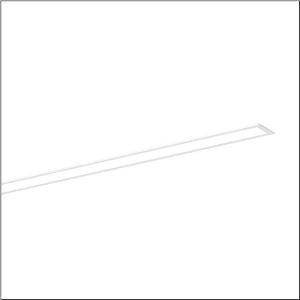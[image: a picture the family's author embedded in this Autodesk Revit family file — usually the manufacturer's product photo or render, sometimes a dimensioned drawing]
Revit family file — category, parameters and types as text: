
# Revit family: silica_r__21_51mx10db32wb_8ee9
name_source: partatom
category: Lighting Fixtures
units: mm (PartAtom-declared; Revit-internal decimal feet)

## family parameters
Cut with Voids When Loaded = No
Host = Face
Light Source = No
Part Type = Normal
Room Calculation Point = No
Round Connector Dimension = Use Diameter
Shared = No

## types (1)
- --- (1 x LED, 3000 lm, 20.2 W, 3000K)
    Apparent Load = 20 VA
    CIE Flux Codes = 48 79 96 100 100
    Color Rendering = 80
    Color Temperature = 3000K
    Default Elevation = 1800 mm
    Description = Silica® 21, office luminaire, primary optical cover: cover, of PMMA, opal, light emission: direct distribution, primary light characteristic: symmetric, installation type: recessed, LED, rated luminous flux: 3.000lm, luminous efficacy: 149lm/W, light colour: 830, colour temperature: 3000K, with terminal, 3+2-pole, max. 2.5mm², mains connection: 220..240V, AC, 50/60Hz, luminaire housing, of aluminium, traffic white (RAL 9016), length: 1.528mm, width: 79mm, height: 53mm, protection rating (complete): IP20, insulation class (complete): insulation class I (protective earthing), certification: CE, permissible operating ambient temperature: 0..+35°C, standard: EN 50419, packaging unit: 1 piece
    Height = 0 mm  [stored 0 ft]
    Lamp = 1 x LED
    Lamp Light Flux = 3000 lm
    Lamp Power = 20.2 W
    Lamp count = 1
    Length = 1527 mm
    Luminous efficacy = 149 lm/W
    Manufacturer = Siteco
    ModVariant = No
    Model = 51MX10DB32WB
    Mounting Place = Ceiling
    Mounting Type = Recessed
    Number of Poles = 1
    OnlyDefault = Yes
    Power Factor = 1
    Product Name = Silica® 21
    Product group = office luminaire | ceiling recessed
    ProductGroupID = 400
    Protection Class = Protection class I
    Protection Degree = IP 20
    RLX_Detail_Level = 1
    RLX_Emergency_Light_Flux = 0 lm
    RLX_Emergency_Type = 0
    RLX_Emergency_Type_DB = No
    RlxData = <blob elided: 20789 chars, md5=8d25ae0b>
    Socket = socket
    Standby Power = 0 W
    System Light Flux = 3000 lm
    System Power = 20 W
    Type Comments = factory setting: luminous flux: 100 % | dim-lin: 254 | 233 mA
    Type Image = l_1335891.jpg
    URL = http://relux.com
    VarID = @adj_086485
    Voltage = 0 V
    Weight = 0.00 kg
    Width = 79 mm

note: [stored X ft] marks values corroborated as IEEE doubles in the binary element streams (Revit-internal decimal feet)

## geometry (parser evidence)
native form markers: Blend x4, Sweep x11
no freeform markers — native parametric forms only
